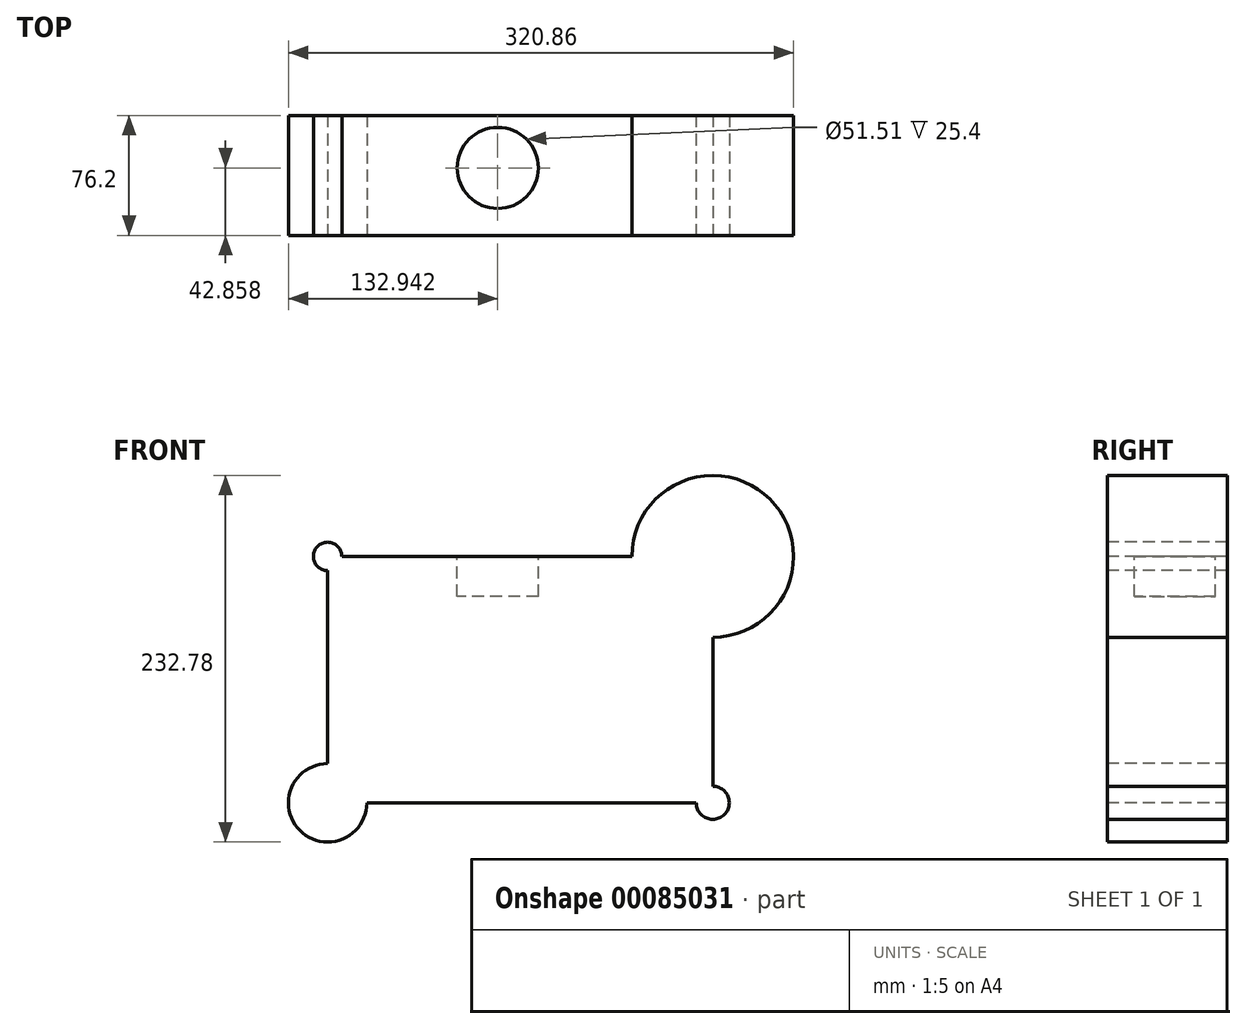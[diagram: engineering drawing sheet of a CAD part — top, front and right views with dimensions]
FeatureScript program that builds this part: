
annotation { "Feature Type Name" : "Feature", "Feature Type Description" : "" }
export const myFeature = defineFeature(function(context is Context, id is Id, definition is map)
    precondition{}
    {
        {
            var Q0;
            Q0=qCreatedBy(makeId("Front.planeOp"),FACE);
            var sketch = newSketch(context, id + "F0", { "sketchPlane" : qUnion([Q0])});
            skLineSegment(sketch, "E0.bottom", {"start": v(-217.06, 53.04) * mm, "end": v(27.54, 53.04) * mm});
            skLineSegment(sketch, "E0.top", {"start": v(-217.06, -103.49) * mm, "end": v(27.54, -103.49) * mm});
            skLineSegment(sketch, "E0.left", {"start": v(-217.06, 53.04) * mm, "end": v(-217.06, -103.49) * mm});
            skLineSegment(sketch, "E0.right", {"start": v(27.54, 53.04) * mm, "end": v(27.54, -103.49) * mm});
            skCircle(sketch, "E1", {"center": v(27.54, 53.04) * mm, "radius": 51.36 * mm});
            skCircle(sketch, "E2", {"center": v(27.54, -103.49) * mm, "radius": 10.5 * mm});
            skCircle(sketch, "E3", {"center": v(-217.06, 53.04) * mm, "radius": 9.04 * mm});
            skCircle(sketch, "E4", {"center": v(-217.06, -103.49) * mm, "radius": 24.9 * mm});
            skSolve(sketch);
        }
        {
            var Q0;
            {var subQ0=sQuery(id+"F0.wireOp",EDGE,"E0.left");var subQ1=sQuery(id+"F0.wireOp",EDGE,"E0.bottom");var subQ2=makeQuery(id+"F0.imprint","INTERSECT",VERTEX,{"derivedFrom":[subQ1,subQ0]});Q0=makeQuery(id+"F0.imprint","IMPRINT",FACE,{"disambiguationData":[TD([[makeQuery(id+"F0.imprint","IMPRINT",EDGE,{"disambiguationData":[TD([[subQ2,-1.0]])],"derivedFrom":subQ1}),1.0]])]});}
            var Q1;
            {var subQ0=sQuery(id+"F0.wireOp",EDGE,"E0.right");var subQ1=sQuery(id+"F0.wireOp",EDGE,"E0.bottom");var subQ2=makeQuery(id+"F0.imprint","INTERSECT",VERTEX,{"derivedFrom":[subQ1,subQ0]});Q1=makeQuery(id+"F0.imprint","IMPRINT",FACE,{"disambiguationData":[TD([[makeQuery(id+"F0.imprint","IMPRINT",EDGE,{"disambiguationData":[TD([[subQ2,1.0]])],"derivedFrom":subQ1}),1.0]])]});}
            var Q2;
            {var subQ0=sQuery(id+"F0.wireOp",EDGE,"E0.left");var subQ1=sQuery(id+"F0.wireOp",EDGE,"E0.top");var subQ2=makeQuery(id+"F0.imprint","INTERSECT",VERTEX,{"derivedFrom":[subQ1,subQ0]});Q2=makeQuery(id+"F0.imprint","IMPRINT",FACE,{"disambiguationData":[TD([[makeQuery(id+"F0.imprint","IMPRINT",EDGE,{"disambiguationData":[TD([[subQ2,-1.0]])],"derivedFrom":subQ1}),-1.0]])]});}
            var Q3;
            {var subQ0=sQuery(id+"F0.wireOp",EDGE,"E0.right");var subQ1=sQuery(id+"F0.wireOp",EDGE,"E0.top");var subQ2=makeQuery(id+"F0.imprint","INTERSECT",VERTEX,{"derivedFrom":[subQ1,subQ0]});Q3=makeQuery(id+"F0.imprint","IMPRINT",FACE,{"disambiguationData":[TD([[makeQuery(id+"F0.imprint","IMPRINT",EDGE,{"disambiguationData":[TD([[subQ2,1.0]])],"derivedFrom":subQ1}),-1.0]])]});}
            var Q4;
            {var subQ0=sQuery(id+"F0.wireOp",EDGE,"E0.left");var subQ1=sQuery(id+"F0.wireOp",EDGE,"E0.bottom");var subQ2=makeQuery(id+"F0.imprint","INTERSECT",VERTEX,{"derivedFrom":[subQ1,subQ0]});Q4=makeQuery(id+"F0.imprint","IMPRINT",FACE,{"disambiguationData":[TD([[makeQuery(id+"F0.imprint","IMPRINT",EDGE,{"disambiguationData":[TD([[subQ2,-1.0]])],"derivedFrom":subQ1}),-1.0]])]});}
            var Q5;
            {var subQ0=sQuery(id+"F0.wireOp",EDGE,"E0.right");var subQ1=sQuery(id+"F0.wireOp",EDGE,"E0.bottom");var subQ2=makeQuery(id+"F0.imprint","INTERSECT",VERTEX,{"derivedFrom":[subQ1,subQ0]});Q5=makeQuery(id+"F0.imprint","IMPRINT",FACE,{"disambiguationData":[TD([[makeQuery(id+"F0.imprint","IMPRINT",EDGE,{"disambiguationData":[TD([[subQ2,1.0]])],"derivedFrom":subQ1}),-1.0]])]});}
            var Q6;
            {var subQ0=sQuery(id+"F0.wireOp",EDGE,"E0.left");var subQ1=sQuery(id+"F0.wireOp",EDGE,"E0.top");var subQ2=makeQuery(id+"F0.imprint","INTERSECT",VERTEX,{"derivedFrom":[subQ1,subQ0]});Q6=makeQuery(id+"F0.imprint","IMPRINT",FACE,{"disambiguationData":[TD([[makeQuery(id+"F0.imprint","IMPRINT",EDGE,{"disambiguationData":[TD([[subQ2,-1.0]])],"derivedFrom":subQ1}),1.0]])]});}
            var Q7;
            {var subQ0=sQuery(id+"F0.wireOp",EDGE,"E0.right");var subQ1=sQuery(id+"F0.wireOp",EDGE,"E0.top");var subQ2=makeQuery(id+"F0.imprint","INTERSECT",VERTEX,{"derivedFrom":[subQ1,subQ0]});Q7=makeQuery(id+"F0.imprint","IMPRINT",FACE,{"disambiguationData":[TD([[makeQuery(id+"F0.imprint","IMPRINT",EDGE,{"disambiguationData":[TD([[subQ2,1.0]])],"derivedFrom":subQ1}),1.0]])]});}
            var Q8;
            {var subQ5=sQuery(id+"F0.wireOp",EDGE,"E3");var subQ13=sQuery(id+"F0.wireOp",EDGE,"E0.bottom");var subQ14=makeQuery(id+"F0.imprint","INTERSECT",VERTEX,{"derivedFrom":[subQ13,subQ5]});Q8=makeQuery(id+"F0.imprint","IMPRINT",FACE,{"disambiguationData":[TD([[makeQuery(id+"F0.imprint","IMPRINT",EDGE,{"disambiguationData":[TD([[subQ14,-1.0]])],"derivedFrom":subQ13}),-1.0]])]});}
            extrude(context, id + "F1", {"entities" : qUnion([Q0, Q1, Q2, Q3, Q4, Q5, Q6, Q7, Q8]), "oppositeDirection" : true, "depth" : 76.2 * mm});
        }
        {
            var Q0;
            Q0=makeQuery(id+"F1.opExtrude","SWEPT_FACE",FACE,{"disambiguationData":[OSD([sQuery(id+"F0.wireOp",EDGE,"E0.bottom")])]});
            var sketch = newSketch(context, id + "F2", { "sketchPlane" : qUnion([Q0])});
            skCircle(sketch, "E5", {"center": v(-109.02, 42.86) * mm, "radius": 25.76 * mm});
            skSolve(sketch);
        }
        {
            var Q0;
            Q0=makeQuery(id+"F2.imprint","IMPRINT",FACE,{"disambiguationData":[TD([[makeQuery(id+"F2.imprint","IMPRINT",EDGE,{"derivedFrom":sQuery(id+"F2.wireOp",EDGE,"E5")}),1.0]])]});
            extrude(context, id + "F3", {"entities" : qUnion([Q0]), "operationType" : NewBodyOperationType.REMOVE, "oppositeDirection" : true, "depth" : 25.4 * mm});
        }
    });
